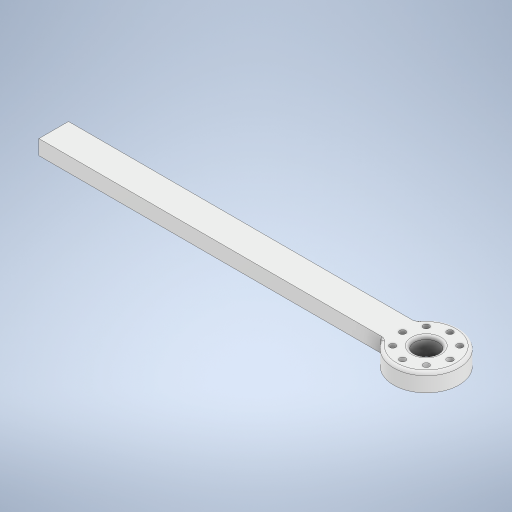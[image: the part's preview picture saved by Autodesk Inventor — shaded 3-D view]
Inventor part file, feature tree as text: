
AUTODESK INVENTOR PART (.ipt)
format: ipt  version: 2024.3 (Build 283343000, 343)  size: 312,320 bytes
history: native  units: mm
features: other x2, extrude x2, sketch x2, fillet x1
ambient origin geometry x8: Origin, YZ Plane, XZ Plane, XY Plane, X Axis, Y Axis, Z Axis, Center Point
bodies: Body1 (feature_tree)
feature tree (7):
  other  "솔리드1"
  extrude  "돌출1"  Depth=80.0mm TaperAngle=360.0deg
  fillet  "모깎기1"  Radius=115.0mm
  extrude  "돌출3"  Depth=5.0mm
  other  "두껍게 하기1"
  sketch  "스케치1"
  sketch  "스케치3"
